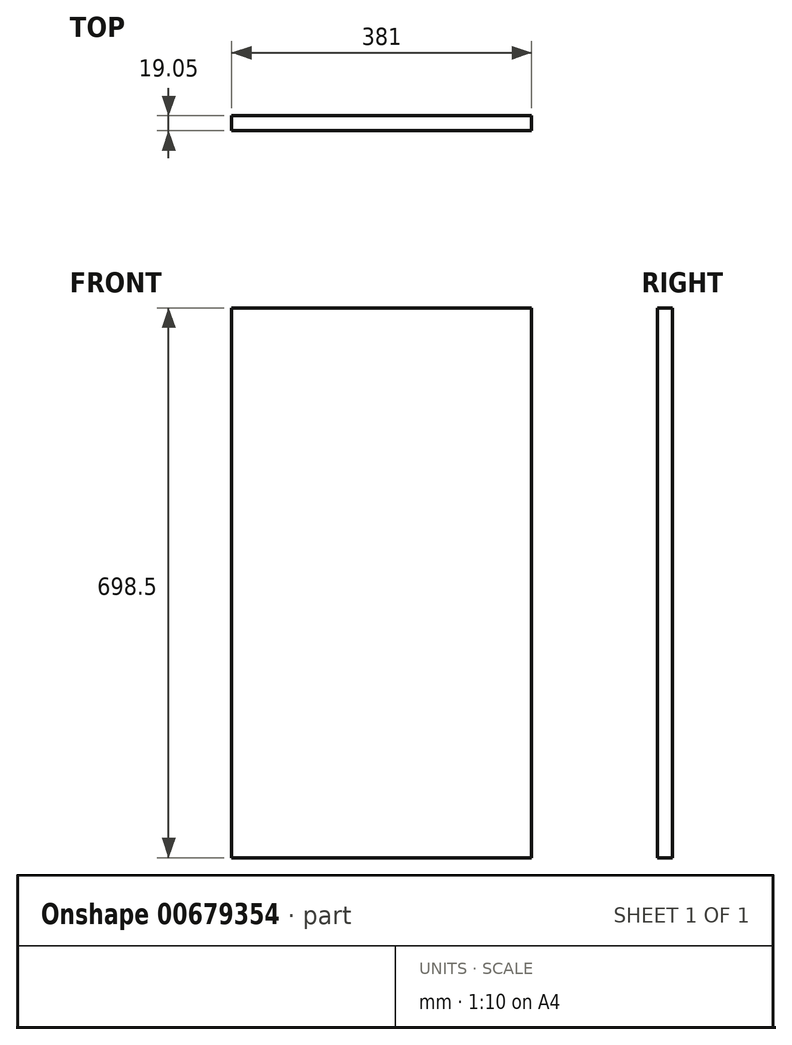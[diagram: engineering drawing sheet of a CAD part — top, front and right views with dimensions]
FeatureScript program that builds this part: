
annotation { "Feature Type Name" : "Feature", "Feature Type Description" : "" }
export const myFeature = defineFeature(function(context is Context, id is Id, definition is map)
    precondition{}
    {
        {
            var Q0;
            Q0=qCreatedBy(makeId("Front.planeOp"),FACE);
            var sketch = newSketch(context, id + "F0", { "sketchPlane" : qUnion([Q0])});
            skLineSegment(sketch, "E0.bottom", {"start": v(190.5, 349.25) * mm, "end": v(-190.5, 349.25) * mm});
            skLineSegment(sketch, "E0.top", {"start": v(190.5, -349.25) * mm, "end": v(-190.5, -349.25) * mm});
            skLineSegment(sketch, "E0.left", {"start": v(190.5, 349.25) * mm, "end": v(190.5, -349.25) * mm});
            skLineSegment(sketch, "E0.right", {"start": v(-190.5, 349.25) * mm, "end": v(-190.5, -349.25) * mm});
            skPoint(sketch, "E0.middle", {"position": v(0, 0) * mm});
            skSolve(sketch);
        }
        {
            var Q0;
            Q0=makeQuery(id+"F0.imprint","IMPRINT",FACE,{"disambiguationData":[TD([[makeQuery(id+"F0.imprint","IMPRINT",EDGE,{"derivedFrom":sQuery(id+"F0.wireOp",EDGE,"E0.bottom")}),1.0]])]});
            extrude(context, id + "F1", {"entities" : qUnion([Q0]), "depth" : 19.05 * mm, "offsetDistance" : 25.4 * mm});
        }
    });
